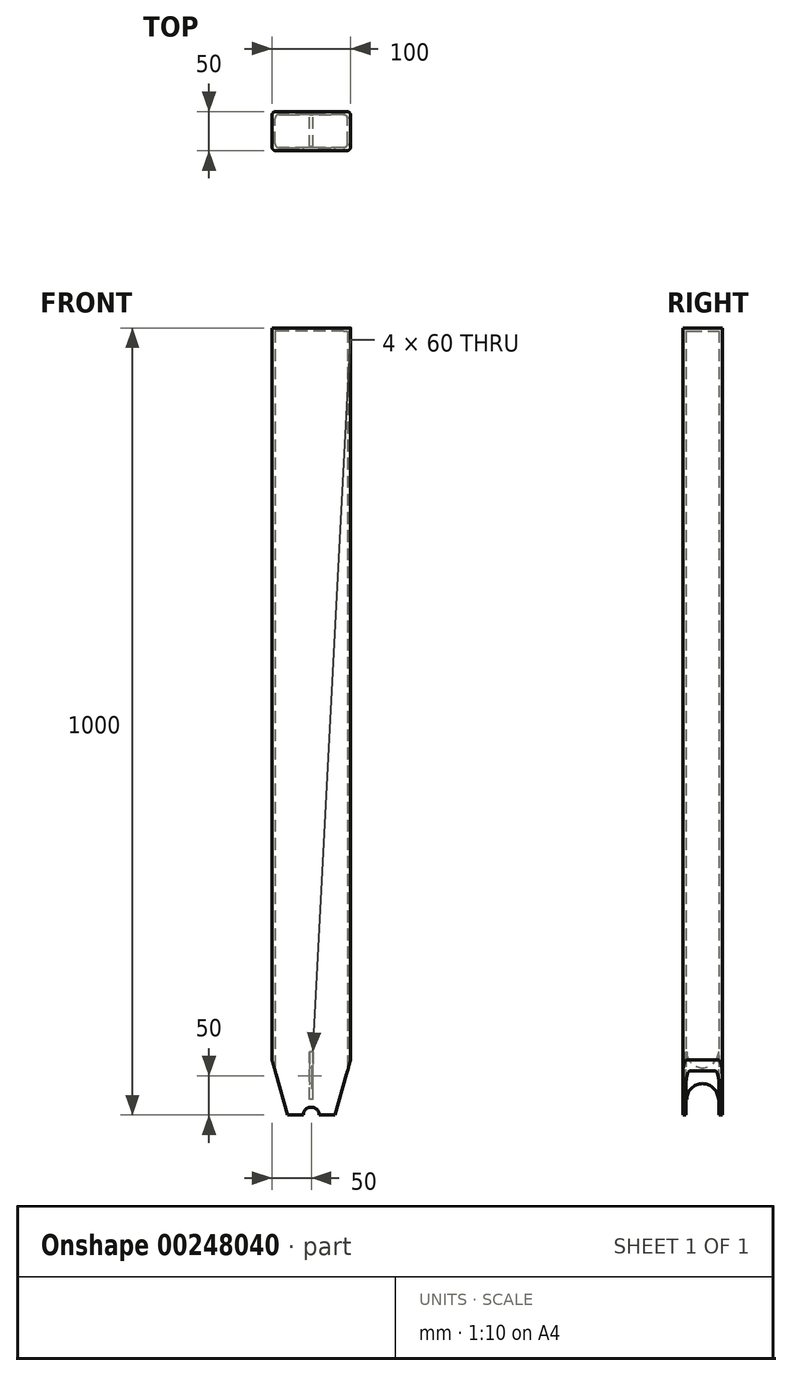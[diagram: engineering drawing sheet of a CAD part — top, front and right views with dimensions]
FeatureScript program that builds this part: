
annotation { "Feature Type Name" : "Feature", "Feature Type Description" : "" }
export const myFeature = defineFeature(function(context is Context, id is Id, definition is map)
    precondition{}
    {
        {
            var Q0;
            Q0=qCreatedBy(makeId("Front.planeOp"),FACE);
            var sketch = newSketch(context, id + "F0", { "sketchPlane" : qUnion([Q0])});
            skLineSegment(sketch, "E0.top", {"start": v(-30, -500) * mm, "end": v(30, -500) * mm});
            skLineSegment(sketch, "E0.left", {"start": v(-50, 500) * mm, "end": v(-50, -430) * mm});
            skLineSegment(sketch, "E0.right", {"start": v(50, 500) * mm, "end": v(50, -430) * mm});
            skPoint(sketch, "E0.middle", {"position": v(0, 0) * mm});
            skPoint(sketch, "E1", {"position": v(-50, -430) * mm});
            skPoint(sketch, "E2", {"position": v(50, -430) * mm});
            skPoint(sketch, "E3", {"position": v(30, -500) * mm});
            skPoint(sketch, "E4", {"position": v(-30, -500) * mm});
            skLineSegment(sketch, "E5", {"start": v(-50, -430) * mm, "end": v(-30, -500) * mm});
            skLineSegment(sketch, "E6", {"start": v(50, -430) * mm, "end": v(30, -500) * mm});
            skPoint(sketch, "E7.orphan", {"position": v(-50, -500) * mm});
            skPoint(sketch, "E8.orphan", {"position": v(50, -500) * mm});
            skLineSegment(sketch, "E9", {"start": v(50, 500) * mm, "end": v(-50, 500) * mm});
            skPoint(sketch, "E0.bottom.start.orphan", {"position": v(-50, 500) * mm});
            skSolve(sketch);
        }
        {
            var Q0;
            Q0=makeQuery(id+"F0.imprint","IMPRINT",FACE,{"disambiguationData":[TD([[makeQuery(id+"F0.imprint","IMPRINT",EDGE,{"derivedFrom":sQuery(id+"F0.wireOp",EDGE,"E0.top")}),1.0]])]});
            extrude(context, id + "F1", {"entities" : qUnion([Q0]), "depth" : 50 * mm, "offsetDistance" : 25 * mm});
        }
        {
            var Q0;
            Q0=makeQuery(id+"F1.opExtrude","SWEPT_FACE",FACE,{"disambiguationData":[OSD([sQuery(id+"F0.wireOp",EDGE,"E0.top")])]});
            var Q1;
            Q1=makeQuery(id+"F1.opExtrude","SWEPT_FACE",FACE,{"disambiguationData":[OSD([sQuery(id+"F0.wireOp",EDGE,"E5")])]});
            var Q2;
            Q2=makeQuery(id+"F1.opExtrude","SWEPT_FACE",FACE,{"disambiguationData":[OSD([sQuery(id+"F0.wireOp",EDGE,"E6")])]});
            shell(context, id + "F2", {"entities" : qUnion([Q0, Q1, Q2]), "thickness" : 4 * mm});
        }
        {
            var Q0;
            Q0=makeQuery(id+"F1.opExtrude","CAP_EDGE",EDGE,{"disambiguationData":[OSD([sQuery(id+"F0.wireOp",EDGE,"E0.right")])],"isStart":false});
            var Q1;
            Q1=makeQuery(id+"F1.opExtrude","CAP_EDGE",EDGE,{"disambiguationData":[OSD([sQuery(id+"F0.wireOp",EDGE,"E0.right")])],"isStart":true});
            var Q2;
            Q2=makeQuery(id+"F1.opExtrude","CAP_EDGE",EDGE,{"disambiguationData":[OSD([sQuery(id+"F0.wireOp",EDGE,"E0.left")])],"isStart":true});
            var Q3;
            Q3=makeQuery(id+"F1.opExtrude","CAP_EDGE",EDGE,{"disambiguationData":[OSD([sQuery(id+"F0.wireOp",EDGE,"E0.left")])],"isStart":false});
            var Q4;
            {var subQ0=sQuery(id+"F0.wireOp",EDGE,"E0.left");Q4=makeQuery(id+"F2.opShell","OFFSET_EDGE",EDGE,{"disambiguationData":[OSD([subQ0]),TDD([makeQuery(id+"F1.opExtrude","CAP_EDGE",EDGE,{"disambiguationData":[OSD([subQ0])],"isStart":true})])]});}
            var Q5;
            {var subQ0=sQuery(id+"F0.wireOp",EDGE,"E0.right");Q5=makeQuery(id+"F2.opShell","OFFSET_EDGE",EDGE,{"disambiguationData":[OSD([subQ0]),TDD([makeQuery(id+"F1.opExtrude","CAP_EDGE",EDGE,{"disambiguationData":[OSD([subQ0])],"isStart":true})])]});}
            var Q6;
            {var subQ0=sQuery(id+"F0.wireOp",EDGE,"E0.right");Q6=makeQuery(id+"F2.opShell","OFFSET_EDGE",EDGE,{"disambiguationData":[OSD([subQ0]),TDD([makeQuery(id+"F1.opExtrude","CAP_EDGE",EDGE,{"disambiguationData":[OSD([subQ0])],"isStart":false})])]});}
            var Q7;
            {var subQ0=sQuery(id+"F0.wireOp",EDGE,"E0.left");Q7=makeQuery(id+"F2.opShell","OFFSET_EDGE",EDGE,{"disambiguationData":[OSD([subQ0]),TDD([makeQuery(id+"F1.opExtrude","CAP_EDGE",EDGE,{"disambiguationData":[OSD([subQ0])],"isStart":false})])]});}
            fillet(context, id + "F3", {"entities" : qUnion([Q0, Q1, Q2, Q3, Q4, Q5, Q6, Q7]), "radius" : 5 * mm, "tangentPropagation" : true, "allowEdgeOverflow" : false});
        }
        {
            var Q0;
            Q0=makeQuery(id+"F1.opExtrude","CAP_FACE",FACE,{"disambiguationData":[OSD([sQuery(id+"F0.wireOp",EDGE,"E0.top"),sQuery(id+"F0.wireOp",EDGE,"E0.left"),sQuery(id+"F0.wireOp",EDGE,"E0.right"),sQuery(id+"F0.wireOp",EDGE,"E5"),sQuery(id+"F0.wireOp",EDGE,"E6"),sQuery(id+"F0.wireOp",EDGE,"E9")])],"isStart":true});
            var sketch = newSketch(context, id + "F4", { "sketchPlane" : qUnion([Q0])});
            skPoint(sketch, "E10", {"position": v(0, -500) * mm});
            skSolve(sketch);
        }
        {
            var Q0;
            Q0=sQuery(id+"F4.wireOp",VERTEX,"E10");
            var Q1;
            Q1=makeQuery(id+"F1.opExtrude","SWEPT_BODY",BODY,{"disambiguationData":[OSD([sQuery(id+"F0.wireOp",EDGE,"E0.top"),sQuery(id+"F0.wireOp",EDGE,"E0.left"),sQuery(id+"F0.wireOp",EDGE,"E0.right"),sQuery(id+"F0.wireOp",EDGE,"E5"),sQuery(id+"F0.wireOp",EDGE,"E6"),sQuery(id+"F0.wireOp",EDGE,"E9")])]});
            hole(context, id + "F5", {"style" : HoleStyle.SIMPLE, "endStyle" : HoleEndStyle.THROUGH, "holeDiameter" : 20 * mm, "tappedDepth" : 12 * mm, "tapClearance" : 3, "locations" : qUnion([Q0]), "scope" : qUnion([Q1])});
        }
        {
            var Q0;
            {var subQ0=sQuery(id+"F0.wireOp",EDGE,"E9");var subQ1=sQuery(id+"F0.wireOp",EDGE,"E6");var subQ2=sQuery(id+"F0.wireOp",EDGE,"E5");var subQ3=sQuery(id+"F0.wireOp",EDGE,"E0.right");var subQ4=sQuery(id+"F0.wireOp",EDGE,"E0.left");var subQ5=sQuery(id+"F0.wireOp",EDGE,"E0.top");Q0=makeQuery(id+"F2.opShell","OFFSET_FACE",FACE,{"disambiguationData":[OSD([subQ5,subQ4,subQ3,subQ2,subQ1,subQ0]),TDD([makeQuery(id+"F1.opExtrude","CAP_FACE",FACE,{"disambiguationData":[OSD([subQ5,subQ4,subQ3,subQ2,subQ1,subQ0])],"isStart":true})])]});}
            var sketch = newSketch(context, id + "F6", { "sketchPlane" : qUnion([Q0])});
            skPoint(sketch, "E11", {"position": v(0, -450) * mm});
            skPoint(sketch, "E11.positionSnap0", {"position": v(0, -490) * mm});
            skLineSegment(sketch, "E12.bottom", {"start": v(2, -480) * mm, "end": v(-2, -480) * mm});
            skLineSegment(sketch, "E12.top", {"start": v(2, -420) * mm, "end": v(-2, -420) * mm});
            skLineSegment(sketch, "E12.left", {"start": v(2, -480) * mm, "end": v(2, -420) * mm});
            skLineSegment(sketch, "E12.right", {"start": v(-2, -480) * mm, "end": v(-2, -420) * mm});
            skSolve(sketch);
        }
        {
            var Q0;
            Q0=makeQuery(id+"F6.imprint","IMPRINT",FACE,{"disambiguationData":[TD([[makeQuery(id+"F6.imprint","IMPRINT",EDGE,{"derivedFrom":sQuery(id+"F6.wireOp",EDGE,"E12.bottom")}),-1.0]])]});
            extrude(context, id + "F7", {"entities" : qUnion([Q0]), "operationType" : NewBodyOperationType.ADD, "depth" : 42 * mm, "offsetDistance" : 25 * mm});
        }
        {
            var Q0;
            Q0=makeQuery(id+"F7.opExtrude","SWEPT_FACE",FACE,{"disambiguationData":[OSD([sQuery(id+"F6.wireOp",EDGE,"E12.right")])]});
            var sketch = newSketch(context, id + "F8", { "sketchPlane" : qUnion([Q0])});
            skPoint(sketch, "E13", {"position": v(25, -480) * mm});
            skPoint(sketch, "E14", {"position": v(25, -420) * mm});
            skSolve(sketch);
        }
        {
            var Q0;
            Q0=sQuery(id+"F8.wireOp",VERTEX,"E13");
            var Q1;
            Q1=sQuery(id+"F8.wireOp",VERTEX,"E14");
            var Q2;
            Q2=makeQuery(id+"F1.opExtrude","SWEPT_BODY",BODY,{"disambiguationData":[OSD([sQuery(id+"F0.wireOp",EDGE,"E0.top"),sQuery(id+"F0.wireOp",EDGE,"E0.left"),sQuery(id+"F0.wireOp",EDGE,"E0.right"),sQuery(id+"F0.wireOp",EDGE,"E5"),sQuery(id+"F0.wireOp",EDGE,"E6"),sQuery(id+"F0.wireOp",EDGE,"E9")])]});
            hole(context, id + "F9", {"style" : HoleStyle.SIMPLE, "endStyle" : HoleEndStyle.BLIND, "holeDiameter" : 40 * mm, "holeDepth" : 4 * mm, "tappedDepth" : 12 * mm, "tapClearance" : 3, "locations" : qUnion([Q0, Q1]), "scope" : qUnion([Q2])});
        }
    });
